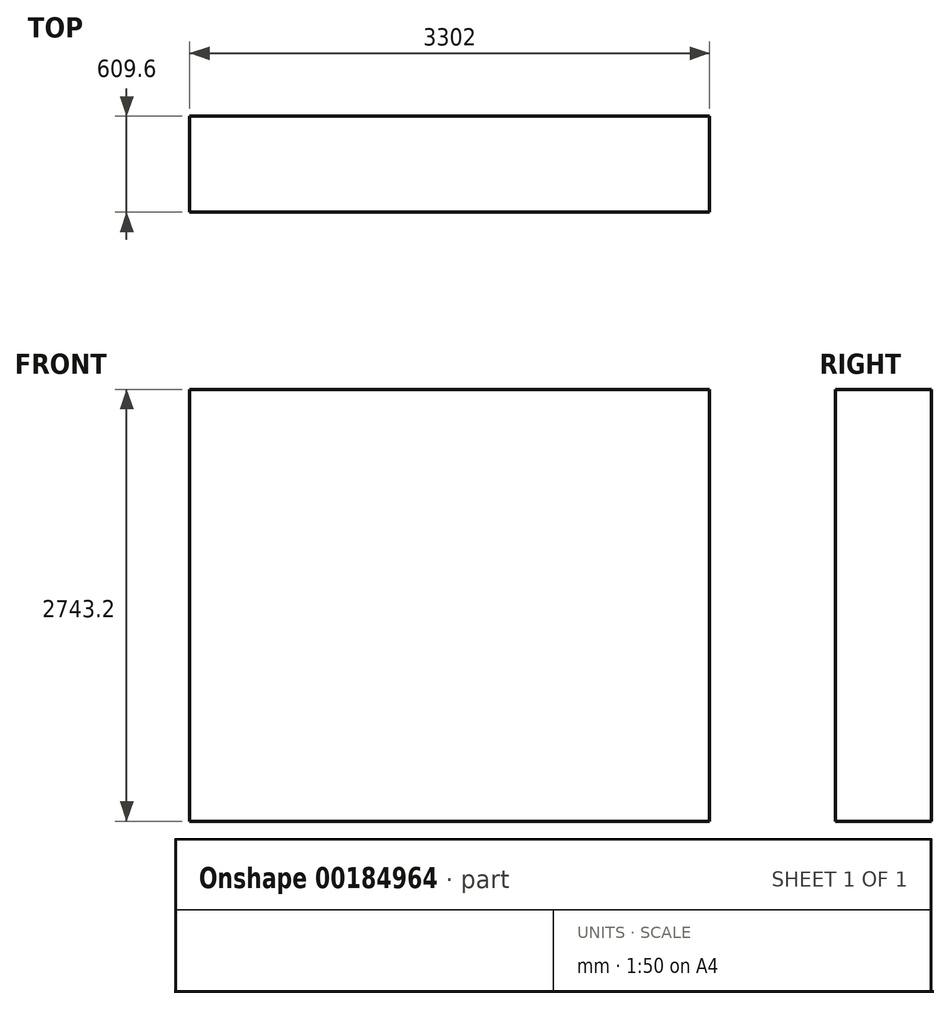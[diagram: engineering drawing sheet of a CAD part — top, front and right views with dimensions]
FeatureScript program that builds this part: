
annotation { "Feature Type Name" : "Feature", "Feature Type Description" : "" }
export const myFeature = defineFeature(function(context is Context, id is Id, definition is map)
    precondition{}
    {
        {
            var Q0;
            Q0=qCreatedBy(makeId("Top.planeOp"),FACE);
            var sketch = newSketch(context, id + "F0", { "sketchPlane" : qUnion([Q0])});
            skLineSegment(sketch, "E0.bottom", {"start": v(1651, 304.8) * mm, "end": v(-1651, 304.8) * mm});
            skLineSegment(sketch, "E0.top", {"start": v(1651, -304.8) * mm, "end": v(-1651, -304.8) * mm});
            skLineSegment(sketch, "E0.left", {"start": v(1651, 304.8) * mm, "end": v(1651, -304.8) * mm});
            skLineSegment(sketch, "E0.right", {"start": v(-1651, 304.8) * mm, "end": v(-1651, -304.8) * mm});
            skPoint(sketch, "E0.middle", {"position": v(0, 0) * mm});
            skSolve(sketch);
        }
        {
            var Q0;
            Q0=makeQuery(id+"F0.imprint","IMPRINT",FACE,{"disambiguationData":[TD([[makeQuery(id+"F0.imprint","IMPRINT",EDGE,{"derivedFrom":sQuery(id+"F0.wireOp",EDGE,"E0.bottom")}),1.0]])]});
            extrude(context, id + "F1", {"entities" : qUnion([Q0]), "depth" : 2743.2 * mm});
        }
    });
